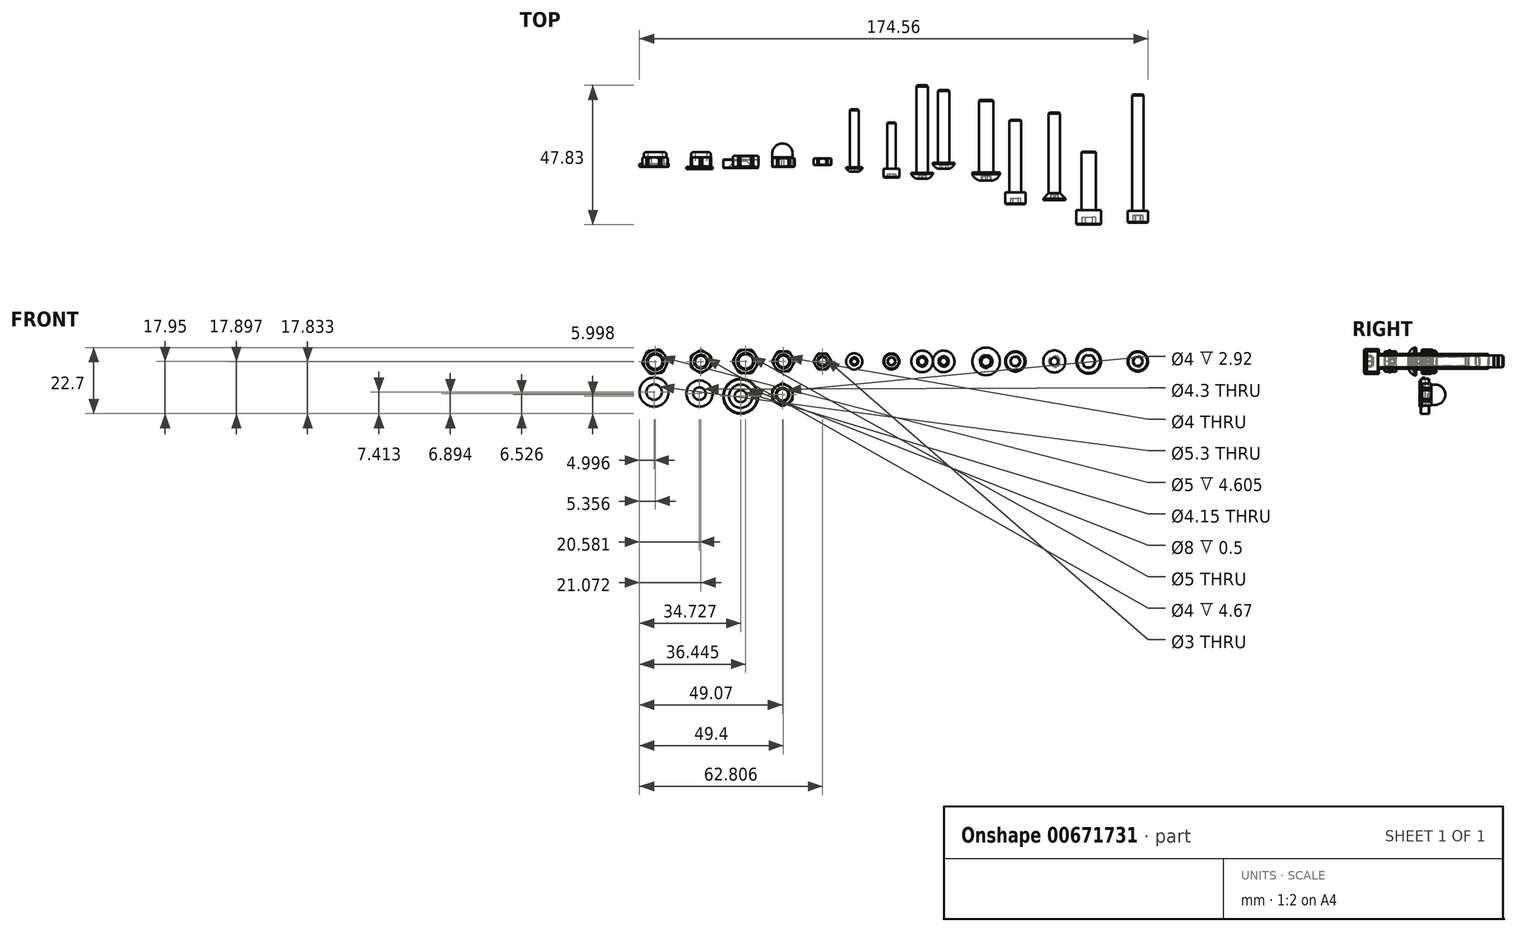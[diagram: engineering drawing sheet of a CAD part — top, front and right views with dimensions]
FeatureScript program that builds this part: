
annotation { "Feature Type Name" : "Feature", "Feature Type Description" : "" }
export const myFeature = defineFeature(function(context is Context, id is Id, definition is map)
    precondition{}
    {
        {
            var Q0;
            Q0=qCreatedBy(makeId("Top.planeOp"),FACE);
            var sketch = newSketch(context, id + "F0", { "sketchPlane" : qUnion([Q0])});
            skLineSegment(sketch, "E0.bottom", {"start": v(-2, 0) * mm, "end": v(-3.83, 0) * mm});
            skLineSegment(sketch, "E0.top", {"start": v(-2, 3) * mm, "end": v(-3.83, 3) * mm});
            skLineSegment(sketch, "E0.left", {"start": v(-2, 0) * mm, "end": v(-2, 3) * mm});
            skLineSegment(sketch, "E0.right", {"start": v(-3.83, 0) * mm, "end": v(-3.83, 3) * mm});
            skLineSegment(sketch, "E1", {"start": v(-2, 0) * mm, "end": v(0, 0) * mm, "construction": true});
            skLineSegment(sketch, "E2", {"start": v(0, 0) * mm, "end": v(0, 3) * mm, "construction": true});
            skSolve(sketch);
        }
        {
            var Q0;
            Q0=qSketchRegion(id+"F0",true);
            var Q1;
            Q1=sQuery(id+"F0.wireOp",EDGE,"E2");
            revolve(context, id + "F1", {"entities" : qUnion([Q0]), "axis" : qUnion([Q1]), "revolveType" : RevolveType.FULL});
        }
        {
            var Q0;
            Q0=makeQuery(id+"F1.opRevolve","SWEPT_EDGE",EDGE,{"disambiguationData":[OSD([sQuery(id+"F0.wireOp",EDGE,"E0.bottom"),sQuery(id+"F0.wireOp",EDGE,"E0.right")])]});
            var Q1;
            Q1=makeQuery(id+"F1.opRevolve","SWEPT_EDGE",EDGE,{"disambiguationData":[OSD([sQuery(id+"F0.wireOp",EDGE,"E0.top"),sQuery(id+"F0.wireOp",EDGE,"E0.right")])]});
            var Q2;
            Q2=makeQuery(id+"F1.opRevolve","SWEPT_EDGE",EDGE,{"disambiguationData":[OSD([sQuery(id+"F0.wireOp",EDGE,"E0.bottom"),sQuery(id+"F0.wireOp",EDGE,"E0.left")])]});
            var Q3;
            Q3=makeQuery(id+"F1.opRevolve","SWEPT_EDGE",EDGE,{"disambiguationData":[OSD([sQuery(id+"F0.wireOp",EDGE,"E0.top"),sQuery(id+"F0.wireOp",EDGE,"E0.left")])]});
            chamfer(context, id + "F2", {"entities" : qUnion([Q0, Q1, Q2, Q3]), "chamferType" : ChamferType.OFFSET_ANGLE, "width" : 0.77 * mm / 2, "oppositeDirection" : false, "angle" : 30 * degree, "tangentPropagation" : true});
        }
        {
            var Q0;
            Q0=makeQuery(id+"F1.opRevolve","SWEPT_FACE",FACE,{"disambiguationData":[OSD([sQuery(id+"F0.wireOp",EDGE,"E0.bottom")])]});
            var sketch = newSketch(context, id + "F3", { "sketchPlane" : qUnion([Q0])});
            skCircle(sketch, "E3.cCircle", {"center": v(0, 0) * mm, "radius": 3.45 * mm, "construction": true});
            skLineSegment(sketch, "E3.0", {"start": v(3.98, 0) * mm, "end": v(2, -3.45) * mm});
            skLineSegment(sketch, "E3.1", {"start": v(2, -3.45) * mm, "end": v(-2, -3.45) * mm});
            skLineSegment(sketch, "E3.2", {"start": v(-2, -3.45) * mm, "end": v(-3.98, 0) * mm});
            skLineSegment(sketch, "E3.3", {"start": v(-3.98, 0) * mm, "end": v(-2, 3.45) * mm});
            skLineSegment(sketch, "E3.4", {"start": v(-2, 3.45) * mm, "end": v(2, 3.45) * mm});
            skLineSegment(sketch, "E3.5", {"start": v(2, 3.45) * mm, "end": v(3.98, 0) * mm});
            skPoint(sketch, "E3.0.midPoint", {"position": v(2.99, -1.73) * mm});
            skCircle(sketch, "E4", {"center": v(0, 0) * mm, "radius": 4.53 * mm});
            skSolve(sketch);
        }
        {
            var Q0;
            Q0=qSketchRegion(id+"F3",true);
            extrude(context, id + "F4", {"entities" : qUnion([Q0]), "operationType" : NewBodyOperationType.REMOVE, "oppositeDirection" : true, "depth" : 25 * mm, "offsetDistance" : 25 * mm});
        }
        {
            var Q0;
            Q0=qCreatedBy(makeId("Top.planeOp"),FACE);
            var sketch = newSketch(context, id + "F5", { "sketchPlane" : qUnion([Q0])});
            skLineSegment(sketch, "E5.bottom", {"start": v(10.4, 2.85) * mm, "end": v(11.9, 2.85) * mm});
            skLineSegment(sketch, "E5.top", {"start": v(10.4, 0.58) * mm, "end": v(11.9, 0.58) * mm});
            skLineSegment(sketch, "E5.left", {"start": v(10.4, 2.85) * mm, "end": v(10.4, 0.58) * mm});
            skLineSegment(sketch, "E5.right", {"start": v(11.9, 2.85) * mm, "end": v(11.9, 0.58) * mm});
            skLineSegment(sketch, "E6", {"start": v(11.9, 0.58) * mm, "end": v(13.4, 0.58) * mm, "construction": true});
            skLineSegment(sketch, "E7", {"start": v(13.4, 0.58) * mm, "end": v(13.4, 2.85) * mm, "construction": true});
            skSolve(sketch);
        }
        {
            var Q0;
            Q0=qSketchRegion(id+"F5",true);
            var Q1;
            Q1=sQuery(id+"F5.wireOp",EDGE,"E7");
            revolve(context, id + "F6", {"entities" : qUnion([Q0]), "axis" : qUnion([Q1]), "revolveType" : RevolveType.FULL});
        }
        {
            var Q0;
            Q0=makeQuery(id+"F6.opRevolve","SWEPT_EDGE",EDGE,{"disambiguationData":[OSD([sQuery(id+"F5.wireOp",EDGE,"E5.top"),sQuery(id+"F5.wireOp",EDGE,"E5.right")])]});
            var Q1;
            Q1=makeQuery(id+"F6.opRevolve","SWEPT_EDGE",EDGE,{"disambiguationData":[OSD([sQuery(id+"F5.wireOp",EDGE,"E5.top"),sQuery(id+"F5.wireOp",EDGE,"E5.left")])]});
            var Q2;
            Q2=makeQuery(id+"F6.opRevolve","SWEPT_EDGE",EDGE,{"disambiguationData":[OSD([sQuery(id+"F5.wireOp",EDGE,"E5.bottom"),sQuery(id+"F5.wireOp",EDGE,"E5.right")])]});
            var Q3;
            Q3=makeQuery(id+"F6.opRevolve","SWEPT_EDGE",EDGE,{"disambiguationData":[OSD([sQuery(id+"F5.wireOp",EDGE,"E5.bottom"),sQuery(id+"F5.wireOp",EDGE,"E5.left")])]});
            chamfer(context, id + "F7", {"entities" : qUnion([Q0, Q1, Q2, Q3]), "width" : 0.51 / 2 * mm, "tangentPropagation" : true});
        }
        {
            var Q0;
            Q0=makeQuery(id+"F6.opRevolve","SWEPT_FACE",FACE,{"disambiguationData":[OSD([sQuery(id+"F5.wireOp",EDGE,"E5.top")])]});
            var sketch = newSketch(context, id + "F8", { "sketchPlane" : qUnion([Q0])});
            skCircle(sketch, "E8.cCircle", {"center": v(13.4, 0) * mm, "radius": 2.75 * mm, "construction": true});
            skLineSegment(sketch, "E8.0", {"start": v(16.58, 0) * mm, "end": v(15, -2.75) * mm});
            skLineSegment(sketch, "E8.1", {"start": v(15, -2.75) * mm, "end": v(11.82, -2.75) * mm});
            skLineSegment(sketch, "E8.2", {"start": v(11.82, -2.75) * mm, "end": v(10.23, 0) * mm});
            skLineSegment(sketch, "E8.3", {"start": v(10.23, 0) * mm, "end": v(11.82, 2.75) * mm});
            skLineSegment(sketch, "E8.4", {"start": v(11.82, 2.75) * mm, "end": v(15, 2.75) * mm});
            skLineSegment(sketch, "E8.5", {"start": v(15, 2.75) * mm, "end": v(16.58, 0) * mm});
            skPoint(sketch, "E8.0.midPoint", {"position": v(15.79, -1.38) * mm});
            skCircle(sketch, "E9", {"center": v(13.4, 0) * mm, "radius": 3.66 * mm});
            skSolve(sketch);
        }
        {
            var Q0;
            Q0=qSketchRegion(id+"F8",true);
            extrude(context, id + "F9", {"entities" : qUnion([Q0]), "operationType" : NewBodyOperationType.REMOVE, "oppositeDirection" : true, "depth" : 25 * mm, "offsetDistance" : 25 * mm});
        }
        {
            var Q0;
            Q0=qCreatedBy(makeId("Top.planeOp"),FACE);
            var sketch = newSketch(context, id + "F10", { "sketchPlane" : qUnion([Q0])});
            skLineSegment(sketch, "E10.bottom", {"start": v(-15.45, 3.8) * mm, "end": v(-17.35, 3.8) * mm});
            skLineSegment(sketch, "E10.top", {"start": v(-15.45, -0.05) * mm, "end": v(-17.35, -0.05) * mm});
            skLineSegment(sketch, "E10.left", {"start": v(-15.45, 3.8) * mm, "end": v(-15.45, -0.05) * mm});
            skLineSegment(sketch, "E10.right", {"start": v(-17.35, 3.8) * mm, "end": v(-17.35, -0.05) * mm});
            skLineSegment(sketch, "E11", {"start": v(-15.45, 3.8) * mm, "end": v(-12.95, 3.8) * mm, "construction": true});
            skLineSegment(sketch, "E12", {"start": v(-12.95, 3.8) * mm, "end": v(-12.95, -0.05) * mm, "construction": true});
            skSolve(sketch);
        }
        {
            var Q0;
            Q0=qSketchRegion(id+"F10",true);
            var Q1;
            Q1=sQuery(id+"F10.wireOp",EDGE,"E12");
            revolve(context, id + "F11", {"entities" : qUnion([Q0]), "axis" : qUnion([Q1]), "revolveType" : RevolveType.FULL});
        }
        {
            var Q0;
            Q0=makeQuery(id+"F11.opRevolve","SWEPT_EDGE",EDGE,{"disambiguationData":[OSD([sQuery(id+"F10.wireOp",EDGE,"E10.bottom"),sQuery(id+"F10.wireOp",EDGE,"E10.left")])]});
            var Q1;
            Q1=makeQuery(id+"F11.opRevolve","SWEPT_EDGE",EDGE,{"disambiguationData":[OSD([sQuery(id+"F10.wireOp",EDGE,"E10.bottom"),sQuery(id+"F10.wireOp",EDGE,"E10.right")])]});
            var Q2;
            Q2=makeQuery(id+"F11.opRevolve","SWEPT_EDGE",EDGE,{"disambiguationData":[OSD([sQuery(id+"F10.wireOp",EDGE,"E10.top"),sQuery(id+"F10.wireOp",EDGE,"E10.left")])]});
            var Q3;
            Q3=makeQuery(id+"F11.opRevolve","SWEPT_EDGE",EDGE,{"disambiguationData":[OSD([sQuery(id+"F10.wireOp",EDGE,"E10.top"),sQuery(id+"F10.wireOp",EDGE,"E10.right")])]});
            chamfer(context, id + "F12", {"entities" : qUnion([Q0, Q1, Q2, Q3]), "width" : 0.4 * mm, "tangentPropagation" : true});
        }
        {
            var Q0;
            Q0=makeQuery(id+"F11.opRevolve","SWEPT_FACE",FACE,{"disambiguationData":[OSD([sQuery(id+"F10.wireOp",EDGE,"E10.top")])]});
            var sketch = newSketch(context, id + "F13", { "sketchPlane" : qUnion([Q0])});
            skCircle(sketch, "E13.cCircle", {"center": v(-12.95, 0) * mm, "radius": 4 * mm, "construction": true});
            skLineSegment(sketch, "E13.0", {"start": v(-8.34, 0) * mm, "end": v(-10.65, -4) * mm});
            skLineSegment(sketch, "E13.1", {"start": v(-10.65, -4) * mm, "end": v(-15.26, -4) * mm});
            skLineSegment(sketch, "E13.2", {"start": v(-15.26, -4) * mm, "end": v(-17.57, 0) * mm});
            skLineSegment(sketch, "E13.3", {"start": v(-17.57, 0) * mm, "end": v(-15.26, 4) * mm});
            skLineSegment(sketch, "E13.4", {"start": v(-15.26, 4) * mm, "end": v(-10.65, 4) * mm});
            skLineSegment(sketch, "E13.5", {"start": v(-10.65, 4) * mm, "end": v(-8.34, 0) * mm});
            skPoint(sketch, "E13.0.midPoint", {"position": v(-9.5, -2) * mm});
            skCircle(sketch, "E14", {"center": v(-12.95, 0) * mm, "radius": 5.32 * mm});
            skSolve(sketch);
        }
        {
            var Q0;
            Q0=qSketchRegion(id+"F13",true);
            extrude(context, id + "F14", {"entities" : qUnion([Q0]), "operationType" : NewBodyOperationType.REMOVE, "oppositeDirection" : true, "depth" : 25 * mm, "offsetDistance" : 25 * mm});
        }
        {
            var Q0;
            Q0=qCreatedBy(makeId("Top.planeOp"),FACE);
            var sketch = newSketch(context, id + "F15", { "sketchPlane" : qUnion([Q0])});
            skLineSegment(sketch, "E15", {"start": v(24.32, 19.82) * mm, "end": v(24.32, -1.7) * mm});
            skLineSegment(sketch, "E16", {"start": v(24.32, -1.7) * mm, "end": v(22.95, -1.7) * mm});
            skLineSegment(sketch, "E17", {"start": v(21.55, -0.58) * mm, "end": v(21.55, -0.18) * mm});
            skLineSegment(sketch, "E18", {"start": v(21.55, -0.18) * mm, "end": v(22.82, -0.18) * mm});
            skLineSegment(sketch, "E19", {"start": v(22.82, -0.18) * mm, "end": v(22.82, 19.41) * mm});
            skLineSegment(sketch, "E20", {"start": v(22.82, 19.41) * mm, "end": v(23.18, 19.82) * mm});
            skLineSegment(sketch, "E21", {"start": v(23.18, 19.82) * mm, "end": v(24.32, 19.82) * mm});
            skArc(sketch, "E22", {"start": v(22.95, -1.7) * mm, "mid": v(22.16, -1.26) * mm, "end": v(21.55, -0.58) * mm});
            skSolve(sketch);
        }
        {
            var Q0;
            Q0=qSketchRegion(id+"F15",true);
            var Q1;
            Q1=sQuery(id+"F15.wireOp",EDGE,"E15");
            revolve(context, id + "F16", {"entities" : qUnion([Q0]), "axis" : qUnion([Q1]), "revolveType" : RevolveType.FULL});
        }
        {
            var Q0;
            Q0=makeQuery(id+"F16.opRevolve","SWEPT_FACE",FACE,{"disambiguationData":[OSD([sQuery(id+"F15.wireOp",EDGE,"E16")])]});
            var sketch = newSketch(context, id + "F17", { "sketchPlane" : qUnion([Q0])});
            skCircle(sketch, "E23.cCircle", {"center": v(24.32, 0) * mm, "radius": 1.02 * mm, "construction": true});
            skLineSegment(sketch, "E23.0", {"start": v(25.34, 0.59) * mm, "end": v(25.34, -0.59) * mm});
            skLineSegment(sketch, "E23.1", {"start": v(25.34, -0.59) * mm, "end": v(24.32, -1.17) * mm});
            skLineSegment(sketch, "E23.2", {"start": v(24.32, -1.17) * mm, "end": v(23.3, -0.59) * mm});
            skLineSegment(sketch, "E23.3", {"start": v(23.3, -0.59) * mm, "end": v(23.3, 0.59) * mm});
            skLineSegment(sketch, "E23.4", {"start": v(23.3, 0.59) * mm, "end": v(24.32, 1.17) * mm});
            skLineSegment(sketch, "E23.5", {"start": v(24.32, 1.17) * mm, "end": v(25.34, 0.59) * mm});
            skPoint(sketch, "E23.0.midPoint", {"position": v(25.34, 0) * mm});
            skSolve(sketch);
        }
        {
            var Q0;
            Q0=qSketchRegion(id+"F17",true);
            extrude(context, id + "F18", {"entities" : qUnion([Q0]), "operationType" : NewBodyOperationType.REMOVE, "oppositeDirection" : true, "depth" : 1.04 * mm, "offsetDistance" : 25 * mm});
        }
        {
            var Q0;
            Q0=qCreatedBy(makeId("Top.planeOp"),FACE);
            var sketch = newSketch(context, id + "F19", { "sketchPlane" : qUnion([Q0])});
            skLineSegment(sketch, "E24.bottom", {"start": v(34.33, -0.72) * mm, "end": v(35.58, -0.72) * mm});
            skLineSegment(sketch, "E24.top", {"start": v(34.61, -3.72) * mm, "end": v(37.08, -3.72) * mm});
            skLineSegment(sketch, "E24.left", {"start": v(34.33, -0.72) * mm, "end": v(34.33, -3.44) * mm});
            skLineSegment(sketch, "E24.right", {"start": v(37.08, -0.72) * mm, "end": v(37.08, -3.72) * mm});
            skLineSegment(sketch, "E25.top", {"start": v(37.08, 15.2) * mm, "end": v(35.86, 15.2) * mm});
            skLineSegment(sketch, "E25.left", {"start": v(37.08, -0.72) * mm, "end": v(37.08, 15.2) * mm});
            skLineSegment(sketch, "E25.right", {"start": v(35.58, -0.72) * mm, "end": v(35.58, 14.92) * mm});
            skLineSegment(sketch, "E26", {"start": v(34.33, -3.44) * mm, "end": v(34.61, -3.72) * mm});
            skLineSegment(sketch, "E27", {"start": v(35.58, 14.92) * mm, "end": v(35.86, 15.2) * mm});
            skSolve(sketch);
        }
        {
            var Q0;
            Q0=qSketchRegion(id+"F19",true);
            var Q1;
            Q1=sQuery(id+"F19.wireOp",EDGE,"E25.left");
            revolve(context, id + "F20", {"entities" : qUnion([Q0]), "axis" : qUnion([Q1]), "revolveType" : RevolveType.FULL});
        }
        {
            var Q0;
            Q0=makeQuery(id+"F20.opRevolve","SWEPT_FACE",FACE,{"disambiguationData":[OSD([sQuery(id+"F19.wireOp",EDGE,"E24.top")])]});
            var sketch = newSketch(context, id + "F21", { "sketchPlane" : qUnion([Q0])});
            skCircle(sketch, "E28.cCircle", {"center": v(37.08, 0) * mm, "radius": 1.25 * mm, "construction": true});
            skLineSegment(sketch, "E28.0", {"start": v(37.8, 1.25) * mm, "end": v(38.52, 0) * mm});
            skLineSegment(sketch, "E28.1", {"start": v(38.52, 0) * mm, "end": v(37.8, -1.25) * mm});
            skLineSegment(sketch, "E28.2", {"start": v(37.8, -1.25) * mm, "end": v(36.36, -1.25) * mm});
            skLineSegment(sketch, "E28.3", {"start": v(36.36, -1.25) * mm, "end": v(35.64, 0) * mm});
            skLineSegment(sketch, "E28.4", {"start": v(35.64, 0) * mm, "end": v(36.36, 1.25) * mm});
            skLineSegment(sketch, "E28.5", {"start": v(36.36, 1.25) * mm, "end": v(37.8, 1.25) * mm});
            skPoint(sketch, "E28.0.midPoint", {"position": v(38.16, 0.62) * mm});
            skSolve(sketch);
        }
        {
            var Q0;
            Q0=qSketchRegion(id+"F21",true);
            extrude(context, id + "F22", {"entities" : qUnion([Q0]), "operationType" : NewBodyOperationType.REMOVE, "oppositeDirection" : true, "depth" : 1.3 * mm, "offsetDistance" : 25 * mm});
        }
        {
            var Q0;
            Q0=qCreatedBy(makeId("Top.planeOp"),FACE);
            var sketch = newSketch(context, id + "F23", { "sketchPlane" : qUnion([Q0])});
            skLineSegment(sketch, "E29", {"start": v(55, 26.35) * mm, "end": v(55, -0.73) * mm});
            skLineSegment(sketch, "E30", {"start": v(55, -0.73) * mm, "end": v(53.25, -0.73) * mm});
            skLineSegment(sketch, "E31", {"start": v(51.3, 0.95) * mm, "end": v(51.3, 1.35) * mm});
            skLineSegment(sketch, "E32", {"start": v(51.3, 1.35) * mm, "end": v(53, 1.35) * mm});
            skLineSegment(sketch, "E33", {"start": v(53, 1.35) * mm, "end": v(53, 25.94) * mm});
            skLineSegment(sketch, "E34", {"start": v(53, 25.94) * mm, "end": v(53.36, 26.35) * mm});
            skLineSegment(sketch, "E35", {"start": v(53.36, 26.35) * mm, "end": v(55, 26.35) * mm});
            skArc(sketch, "E36", {"start": v(53.25, -0.73) * mm, "mid": v(52.07, -0.12) * mm, "end": v(51.3, 0.95) * mm});
            skSolve(sketch);
        }
        {
            var Q0;
            Q0=qSketchRegion(id+"F23",true);
            var Q1;
            Q1=sQuery(id+"F23.wireOp",EDGE,"E29");
            revolve(context, id + "F24", {"entities" : qUnion([Q0]), "axis" : qUnion([Q1]), "revolveType" : RevolveType.FULL});
        }
        {
            var Q0;
            Q0=makeQuery(id+"F24.opRevolve","SWEPT_FACE",FACE,{"disambiguationData":[OSD([sQuery(id+"F23.wireOp",EDGE,"E30")])]});
            var sketch = newSketch(context, id + "F25", { "sketchPlane" : qUnion([Q0])});
            skCircle(sketch, "E37.cCircle", {"center": v(55, 0) * mm, "radius": 1.27 * mm, "construction": true});
            skLineSegment(sketch, "E37.0", {"start": v(56.47, 0) * mm, "end": v(55.73, -1.27) * mm});
            skLineSegment(sketch, "E37.1", {"start": v(55.73, -1.27) * mm, "end": v(54.27, -1.27) * mm});
            skLineSegment(sketch, "E37.2", {"start": v(54.27, -1.27) * mm, "end": v(53.53, 0) * mm});
            skLineSegment(sketch, "E37.3", {"start": v(53.53, 0) * mm, "end": v(54.27, 1.27) * mm});
            skLineSegment(sketch, "E37.4", {"start": v(54.27, 1.27) * mm, "end": v(55.73, 1.27) * mm});
            skLineSegment(sketch, "E37.5", {"start": v(55.73, 1.27) * mm, "end": v(56.47, 0) * mm});
            skPoint(sketch, "E37.0.midPoint", {"position": v(56.1, -0.64) * mm});
            skSolve(sketch);
        }
        {
            var Q0;
            Q0=qSketchRegion(id+"F25",true);
            extrude(context, id + "F26", {"entities" : qUnion([Q0]), "operationType" : NewBodyOperationType.REMOVE, "oppositeDirection" : true, "depth" : 1.3 * mm, "offsetDistance" : 25 * mm});
        }
        {
            var Q0;
            Q0=qCreatedBy(makeId("Top.planeOp"),FACE);
            var sketch = newSketch(context, id + "F27", { "sketchPlane" : qUnion([Q0])});
            skLineSegment(sketch, "E38.bottom", {"start": v(76.11, -8.88) * mm, "end": v(77.61, -8.88) * mm});
            skLineSegment(sketch, "E38.top", {"start": v(76.4, -12.88) * mm, "end": v(79.61, -12.88) * mm});
            skLineSegment(sketch, "E38.left", {"start": v(76.11, -8.88) * mm, "end": v(76.11, -12.6) * mm});
            skLineSegment(sketch, "E38.right", {"start": v(79.61, -8.88) * mm, "end": v(79.61, -12.88) * mm});
            skLineSegment(sketch, "E39.top", {"start": v(79.61, 16.12) * mm, "end": v(77.9, 16.12) * mm});
            skLineSegment(sketch, "E39.left", {"start": v(79.61, -8.88) * mm, "end": v(79.61, 16.12) * mm});
            skLineSegment(sketch, "E39.right", {"start": v(77.61, -8.88) * mm, "end": v(77.61, 15.84) * mm});
            skLineSegment(sketch, "E40", {"start": v(76.11, -12.6) * mm, "end": v(76.4, -12.88) * mm});
            skLineSegment(sketch, "E41", {"start": v(77.61, 15.84) * mm, "end": v(77.9, 16.12) * mm});
            skSolve(sketch);
        }
        {
            var Q0;
            Q0=qSketchRegion(id+"F27",true);
            var Q1;
            Q1=sQuery(id+"F27.wireOp",EDGE,"E39.left");
            revolve(context, id + "F28", {"entities" : qUnion([Q0]), "axis" : qUnion([Q1]), "revolveType" : RevolveType.FULL});
        }
        {
            var Q0;
            Q0=makeQuery(id+"F28.opRevolve","SWEPT_FACE",FACE,{"disambiguationData":[OSD([sQuery(id+"F27.wireOp",EDGE,"E38.top")])]});
            var sketch = newSketch(context, id + "F29", { "sketchPlane" : qUnion([Q0])});
            skCircle(sketch, "E42.cCircle", {"center": v(79.61, 0) * mm, "radius": 1.5 * mm, "construction": true});
            skLineSegment(sketch, "E42.0", {"start": v(81.34, 0) * mm, "end": v(80.48, -1.5) * mm});
            skLineSegment(sketch, "E42.1", {"start": v(80.48, -1.5) * mm, "end": v(78.75, -1.5) * mm});
            skLineSegment(sketch, "E42.2", {"start": v(78.75, -1.5) * mm, "end": v(77.88, 0) * mm});
            skLineSegment(sketch, "E42.3", {"start": v(77.88, 0) * mm, "end": v(78.75, 1.5) * mm});
            skLineSegment(sketch, "E42.4", {"start": v(78.75, 1.5) * mm, "end": v(80.48, 1.5) * mm});
            skLineSegment(sketch, "E42.5", {"start": v(80.48, 1.5) * mm, "end": v(81.34, 0) * mm});
            skPoint(sketch, "E42.0.midPoint", {"position": v(80.91, -0.75) * mm});
            skSolve(sketch);
        }
        {
            var Q0;
            Q0=qSketchRegion(id+"F29",true);
            extrude(context, id + "F30", {"entities" : qUnion([Q0]), "operationType" : NewBodyOperationType.REMOVE, "oppositeDirection" : true, "depth" : 2 * mm, "offsetDistance" : 25 * mm});
        }
        {
            var Q0;
            Q0=qCreatedBy(makeId("Top.planeOp"),FACE);
            var sketch = newSketch(context, id + "F31", { "sketchPlane" : qUnion([Q0])});
            skLineSegment(sketch, "E43.bottom", {"start": v(100.55, -14.88) * mm, "end": v(102.3, -14.88) * mm});
            skLineSegment(sketch, "E43.top", {"start": v(100.83, -19.88) * mm, "end": v(104.8, -19.88) * mm});
            skLineSegment(sketch, "E43.left", {"start": v(100.55, -14.88) * mm, "end": v(100.55, -19.6) * mm});
            skLineSegment(sketch, "E43.right", {"start": v(104.8, -14.88) * mm, "end": v(104.8, -19.88) * mm});
            skLineSegment(sketch, "E44.top", {"start": v(104.8, 5.12) * mm, "end": v(102.58, 5.12) * mm});
            skLineSegment(sketch, "E44.left", {"start": v(104.8, -14.88) * mm, "end": v(104.8, 5.12) * mm});
            skLineSegment(sketch, "E44.right", {"start": v(102.3, -14.88) * mm, "end": v(102.3, 4.84) * mm});
            skLineSegment(sketch, "E45", {"start": v(100.55, -19.6) * mm, "end": v(100.83, -19.88) * mm});
            skLineSegment(sketch, "E46", {"start": v(102.3, 4.84) * mm, "end": v(102.58, 5.12) * mm});
            skSolve(sketch);
        }
        {
            var Q0;
            Q0=qSketchRegion(id+"F31",true);
            var Q1;
            Q1=sQuery(id+"F31.wireOp",EDGE,"E43.right");
            revolve(context, id + "F32", {"entities" : qUnion([Q0]), "axis" : qUnion([Q1]), "revolveType" : RevolveType.FULL});
        }
        {
            var Q0;
            Q0=makeQuery(id+"F32.opRevolve","SWEPT_FACE",FACE,{"disambiguationData":[OSD([sQuery(id+"F31.wireOp",EDGE,"E43.top")])]});
            var sketch = newSketch(context, id + "F33", { "sketchPlane" : qUnion([Q0])});
            skCircle(sketch, "E47.cCircle", {"center": v(104.8, 0) * mm, "radius": 2 * mm, "construction": true});
            skLineSegment(sketch, "E47.0", {"start": v(107.1, 0) * mm, "end": v(105.95, -2) * mm});
            skLineSegment(sketch, "E47.1", {"start": v(105.95, -2) * mm, "end": v(103.64, -2) * mm});
            skLineSegment(sketch, "E47.2", {"start": v(103.64, -2) * mm, "end": v(102.49, 0) * mm});
            skLineSegment(sketch, "E47.3", {"start": v(102.49, 0) * mm, "end": v(103.64, 2) * mm});
            skLineSegment(sketch, "E47.4", {"start": v(103.64, 2) * mm, "end": v(105.95, 2) * mm});
            skLineSegment(sketch, "E47.5", {"start": v(105.95, 2) * mm, "end": v(107.1, 0) * mm});
            skPoint(sketch, "E47.0.midPoint", {"position": v(106.53, -1) * mm});
            skSolve(sketch);
        }
        {
            var Q0;
            Q0=qSketchRegion(id+"F33",true);
            extrude(context, id + "F34", {"entities" : qUnion([Q0]), "operationType" : NewBodyOperationType.REMOVE, "oppositeDirection" : true, "depth" : 2.5 * mm, "offsetDistance" : 25 * mm});
        }
        {
            var Q0;
            Q0=qCreatedBy(makeId("Top.planeOp"),FACE);
            var sketch = newSketch(context, id + "F35", { "sketchPlane" : qUnion([Q0])});
            skLineSegment(sketch, "E48.bottom", {"start": v(118.16, -15.2) * mm, "end": v(119.66, -15.2) * mm});
            skLineSegment(sketch, "E48.top", {"start": v(118.45, -19.2) * mm, "end": v(121.66, -19.2) * mm});
            skLineSegment(sketch, "E48.left", {"start": v(118.16, -15.2) * mm, "end": v(118.16, -18.93) * mm});
            skLineSegment(sketch, "E48.right", {"start": v(121.66, -15.2) * mm, "end": v(121.66, -19.2) * mm});
            skLineSegment(sketch, "E49.top", {"start": v(121.66, 24.8) * mm, "end": v(119.95, 24.8) * mm});
            skLineSegment(sketch, "E49.left", {"start": v(121.66, -15.2) * mm, "end": v(121.66, 24.8) * mm});
            skLineSegment(sketch, "E49.right", {"start": v(119.66, -15.2) * mm, "end": v(119.66, 24.5) * mm});
            skLineSegment(sketch, "E50", {"start": v(118.16, -18.93) * mm, "end": v(118.45, -19.2) * mm});
            skLineSegment(sketch, "E51", {"start": v(119.66, 24.5) * mm, "end": v(119.95, 24.8) * mm});
            skSolve(sketch);
        }
        {
            var Q0;
            Q0=qSketchRegion(id+"F35",true);
            var Q1;
            Q1=sQuery(id+"F35.wireOp",EDGE,"E49.left");
            revolve(context, id + "F36", {"entities" : qUnion([Q0]), "axis" : qUnion([Q1]), "revolveType" : RevolveType.FULL});
        }
        {
            var Q0;
            Q0=makeQuery(id+"F36.opRevolve","SWEPT_FACE",FACE,{"disambiguationData":[OSD([sQuery(id+"F35.wireOp",EDGE,"E48.top")])]});
            var sketch = newSketch(context, id + "F37", { "sketchPlane" : qUnion([Q0])});
            skCircle(sketch, "E52.cCircle", {"center": v(121.66, 0) * mm, "radius": 1.5 * mm, "construction": true});
            skLineSegment(sketch, "E52.0", {"start": v(122.62, 1.44) * mm, "end": v(123.4, -0.1) * mm});
            skLineSegment(sketch, "E52.1", {"start": v(123.4, -0.1) * mm, "end": v(122.43, -1.55) * mm});
            skLineSegment(sketch, "E52.2", {"start": v(122.43, -1.55) * mm, "end": v(120.7, -1.44) * mm});
            skLineSegment(sketch, "E52.3", {"start": v(120.7, -1.44) * mm, "end": v(119.94, 0.1) * mm});
            skLineSegment(sketch, "E52.4", {"start": v(119.94, 0.1) * mm, "end": v(120.9, 1.55) * mm});
            skLineSegment(sketch, "E52.5", {"start": v(120.9, 1.55) * mm, "end": v(122.62, 1.44) * mm});
            skPoint(sketch, "E52.0.midPoint", {"position": v(123, 0.67) * mm});
            skSolve(sketch);
        }
        {
            var Q0;
            Q0=qSketchRegion(id+"F37",true);
            extrude(context, id + "F38", {"entities" : qUnion([Q0]), "operationType" : NewBodyOperationType.REMOVE, "oppositeDirection" : true, "depth" : 2.5 * mm, "offsetDistance" : 25 * mm});
        }
        {
            var Q0;
            Q0=qCreatedBy(makeId("Front.planeOp"),FACE);
            var sketch = newSketch(context, id + "F39", { "sketchPlane" : qUnion([Q0])});
            skCircle(sketch, "E53", {"center": v(-28.33, -0.05) * mm, "radius": 3.83 * mm});
            skCircle(sketch, "E54", {"center": v(-28.33, -0.05) * mm, "radius": 2 * mm});
            skSolve(sketch);
        }
        {
            var Q0;
            Q0=qSketchRegion(id+"F39",true);
            extrude(context, id + "F40", {"entities" : qUnion([Q0]), "oppositeDirection" : true, "depth" : 3.25 * mm, "offsetDistance" : 25 * mm});
        }
        {
            var Q0;
            Q0=makeQuery(id+"F40.opExtrude","CAP_EDGE",EDGE,{"disambiguationData":[OSD([sQuery(id+"F39.wireOp",EDGE,"E53")])],"isStart":false});
            var Q1;
            Q1=makeQuery(id+"F40.opExtrude","CAP_EDGE",EDGE,{"disambiguationData":[OSD([sQuery(id+"F39.wireOp",EDGE,"E53")])],"isStart":true});
            var Q2;
            Q2=makeQuery(id+"F40.opExtrude","CAP_EDGE",EDGE,{"disambiguationData":[OSD([sQuery(id+"F39.wireOp",EDGE,"E54")])],"isStart":true});
            chamfer(context, id + "F41", {"entities" : qUnion([Q0, Q1, Q2]), "width" : 0.66 / 2 * mm, "tangentPropagation" : true});
        }
        {
            var Q0;
            Q0=makeQuery(id+"F40.opExtrude","CAP_FACE",FACE,{"disambiguationData":[OSD([sQuery(id+"F39.wireOp",EDGE,"E53"),sQuery(id+"F39.wireOp",EDGE,"E54")])],"isStart":false});
            var sketch = newSketch(context, id + "F42", { "sketchPlane" : qUnion([Q0])});
            skCircle(sketch, "E55.cCircle", {"center": v(28.33, -0.05) * mm, "radius": 3.5 * mm, "construction": true});
            skLineSegment(sketch, "E55.0", {"start": v(31.83, 1.97) * mm, "end": v(31.83, -2.07) * mm});
            skLineSegment(sketch, "E55.1", {"start": v(31.83, -2.07) * mm, "end": v(28.33, -4.1) * mm});
            skLineSegment(sketch, "E55.2", {"start": v(28.33, -4.1) * mm, "end": v(24.83, -2.07) * mm});
            skLineSegment(sketch, "E55.3", {"start": v(24.83, -2.07) * mm, "end": v(24.83, 1.97) * mm});
            skLineSegment(sketch, "E55.4", {"start": v(24.83, 1.97) * mm, "end": v(28.33, 3.99) * mm});
            skLineSegment(sketch, "E55.5", {"start": v(28.33, 3.99) * mm, "end": v(31.83, 1.97) * mm});
            skPoint(sketch, "E55.0.midPoint", {"position": v(31.83, -0.05) * mm});
            skCircle(sketch, "E56", {"center": v(28.33, -0.05) * mm, "radius": 6.48 * mm});
            skSolve(sketch);
        }
        {
            var Q0;
            Q0=qSketchRegion(id+"F42",true);
            extrude(context, id + "F43", {"entities" : qUnion([Q0]), "operationType" : NewBodyOperationType.REMOVE, "oppositeDirection" : true, "depth" : 25 * mm, "offsetDistance" : 25 * mm});
        }
        {
            var Q0;
            Q0=makeQuery(id+"F40.opExtrude","CAP_FACE",FACE,{"disambiguationData":[OSD([sQuery(id+"F39.wireOp",EDGE,"E53"),sQuery(id+"F39.wireOp",EDGE,"E54")])],"isStart":false});
            var sketch = newSketch(context, id + "F44", { "sketchPlane" : qUnion([Q0])});
            skCircle(sketch, "E57", {"center": v(28.33, -0.05) * mm, "radius": 2 * mm});
            skCircle(sketch, "E58", {"center": v(28.33, -0.05) * mm, "radius": 3.38 * mm});
            skSolve(sketch);
        }
        {
            var Q0;
            Q0=qSketchRegion(id+"F44",true);
            extrude(context, id + "F45", {"entities" : qUnion([Q0]), "operationType" : NewBodyOperationType.ADD, "depth" : (5 - 3.25) * mm, "offsetDistance" : 25 * mm});
        }
        {
            var Q0;
            Q0=makeQuery(id+"F45.opExtrude","CAP_EDGE",EDGE,{"disambiguationData":[OSD([sQuery(id+"F44.wireOp",EDGE,"E58")])],"isStart":false});
            fillet(context, id + "F46", {"entities" : qUnion([Q0]), "radius" : 0.75 * mm, "tangentPropagation" : true, "allowEdgeOverflow" : false});
        }
        {
            var Q0;
            Q0=qCreatedBy(makeId("Top.planeOp"),FACE);
            var sketch = newSketch(context, id + "F47", { "sketchPlane" : qUnion([Q0])});
            skLineSegment(sketch, "E59", {"start": v(69.58, 22.98) * mm, "end": v(69.58, -4.77) * mm});
            skLineSegment(sketch, "E60", {"start": v(69.58, -4.77) * mm, "end": v(67.48, -4.77) * mm});
            skLineSegment(sketch, "E61", {"start": v(64.83, -2.62) * mm, "end": v(64.83, -2.02) * mm});
            skLineSegment(sketch, "E62", {"start": v(64.83, -2.02) * mm, "end": v(67.08, -2.02) * mm});
            skLineSegment(sketch, "E63", {"start": v(67.08, -2.02) * mm, "end": v(67.08, 22.58) * mm});
            skLineSegment(sketch, "E64", {"start": v(67.08, 22.58) * mm, "end": v(67.44, 22.98) * mm});
            skLineSegment(sketch, "E65", {"start": v(67.44, 22.98) * mm, "end": v(69.58, 22.98) * mm});
            skArc(sketch, "E66", {"start": v(67.48, -4.77) * mm, "mid": v(65.88, -4.03) * mm, "end": v(64.83, -2.62) * mm});
            skSolve(sketch);
        }
        {
            var Q0;
            Q0=makeQuery(id+"F47.imprint","IMPRINT",FACE,{"disambiguationData":[TD([[makeQuery(id+"F47.imprint","IMPRINT",EDGE,{"derivedFrom":sQuery(id+"F47.wireOp",EDGE,"E59")}),-1.0]])]});
            var Q1;
            Q1=sQuery(id+"F47.wireOp",EDGE,"E59");
            revolve(context, id + "F48", {"entities" : qUnion([Q0]), "axis" : qUnion([Q1]), "revolveType" : RevolveType.FULL});
        }
        {
            var Q0;
            Q0=makeQuery(id+"F48.opRevolve","SWEPT_FACE",FACE,{"disambiguationData":[OSD([sQuery(id+"F47.wireOp",EDGE,"E60")])]});
            var sketch = newSketch(context, id + "F49", { "sketchPlane" : qUnion([Q0])});
            skCircle(sketch, "E67.cCircle", {"center": v(69.58, 0) * mm, "radius": 1.5 * mm, "construction": true});
            skLineSegment(sketch, "E67.0", {"start": v(69.92, 1.7) * mm, "end": v(71.22, 0.55) * mm});
            skLineSegment(sketch, "E67.1", {"start": v(71.22, 0.55) * mm, "end": v(70.88, -1.14) * mm});
            skLineSegment(sketch, "E67.2", {"start": v(70.88, -1.14) * mm, "end": v(69.24, -1.7) * mm});
            skLineSegment(sketch, "E67.3", {"start": v(69.24, -1.7) * mm, "end": v(67.94, -0.55) * mm});
            skLineSegment(sketch, "E67.4", {"start": v(67.94, -0.55) * mm, "end": v(68.28, 1.14) * mm});
            skLineSegment(sketch, "E67.5", {"start": v(68.28, 1.14) * mm, "end": v(69.92, 1.7) * mm});
            skPoint(sketch, "E67.0.midPoint", {"position": v(70.57, 1.13) * mm});
            skSolve(sketch);
        }
        {
            var Q0;
            Q0=qSketchRegion(id+"F49",true);
            extrude(context, id + "F50", {"entities" : qUnion([Q0]), "operationType" : NewBodyOperationType.REMOVE, "oppositeDirection" : true, "depth" : 1.56 * mm, "offsetDistance" : 25 * mm});
        }
        {
            var Q0;
            Q0=qCreatedBy(makeId("Front.planeOp"),FACE);
            var sketch = newSketch(context, id + "F51", { "sketchPlane" : qUnion([Q0])});
            skCircle(sketch, "E68", {"center": v(-44.04, -0.12) * mm, "radius": 4.4 * mm});
            skCircle(sketch, "E69", {"center": v(-44.04, -0.12) * mm, "radius": 2.5 * mm});
            skSolve(sketch);
        }
        {
            var Q0;
            Q0=qSketchRegion(id+"F51",true);
            extrude(context, id + "F52", {"entities" : qUnion([Q0]), "oppositeDirection" : true, "depth" : 3.25 * mm, "offsetDistance" : 25 * mm});
        }
        {
            var Q0;
            Q0=makeQuery(id+"F52.opExtrude","CAP_EDGE",EDGE,{"disambiguationData":[OSD([sQuery(id+"F51.wireOp",EDGE,"E68")])],"isStart":false});
            var Q1;
            Q1=makeQuery(id+"F52.opExtrude","CAP_EDGE",EDGE,{"disambiguationData":[OSD([sQuery(id+"F51.wireOp",EDGE,"E68")])],"isStart":true});
            var Q2;
            Q2=makeQuery(id+"F52.opExtrude","CAP_EDGE",EDGE,{"disambiguationData":[OSD([sQuery(id+"F51.wireOp",EDGE,"E69")])],"isStart":true});
            chamfer(context, id + "F53", {"entities" : qUnion([Q0, Q1, Q2]), "width" : (0.79 / 2) * mm, "tangentPropagation" : true});
        }
        {
            var Q0;
            Q0=makeQuery(id+"F52.opExtrude","CAP_FACE",FACE,{"disambiguationData":[OSD([sQuery(id+"F51.wireOp",EDGE,"E68"),sQuery(id+"F51.wireOp",EDGE,"E69")])],"isStart":false});
            var sketch = newSketch(context, id + "F54", { "sketchPlane" : qUnion([Q0])});
            skCircle(sketch, "E70.cCircle", {"center": v(44.04, -0.12) * mm, "radius": 4 * mm, "construction": true});
            skLineSegment(sketch, "E70.0", {"start": v(39.46, 0.47) * mm, "end": v(42.26, 4.14) * mm});
            skLineSegment(sketch, "E70.1", {"start": v(42.26, 4.14) * mm, "end": v(46.84, 3.56) * mm});
            skLineSegment(sketch, "E70.2", {"start": v(46.84, 3.56) * mm, "end": v(48.63, -0.7) * mm});
            skLineSegment(sketch, "E70.3", {"start": v(48.63, -0.7) * mm, "end": v(45.83, -4.38) * mm});
            skLineSegment(sketch, "E70.4", {"start": v(45.83, -4.38) * mm, "end": v(41.25, -3.8) * mm});
            skLineSegment(sketch, "E70.5", {"start": v(41.25, -3.8) * mm, "end": v(39.46, 0.47) * mm});
            skPoint(sketch, "E70.0.midPoint", {"position": v(40.86, 2.3) * mm});
            skCircle(sketch, "E71", {"center": v(44.04, -0.12) * mm, "radius": 6.63 * mm});
            skSolve(sketch);
        }
        {
            var Q0;
            Q0=qSketchRegion(id+"F54",true);
            extrude(context, id + "F55", {"entities" : qUnion([Q0]), "operationType" : NewBodyOperationType.REMOVE, "oppositeDirection" : true, "depth" : 25 * mm, "offsetDistance" : 25 * mm});
        }
        {
            var Q0;
            Q0=makeQuery(id+"F52.opExtrude","CAP_FACE",FACE,{"disambiguationData":[OSD([sQuery(id+"F51.wireOp",EDGE,"E68"),sQuery(id+"F51.wireOp",EDGE,"E69")])],"isStart":false});
            var sketch = newSketch(context, id + "F56", { "sketchPlane" : qUnion([Q0])});
            skCircle(sketch, "E72", {"center": v(44.04, -0.12) * mm, "radius": 2.5 * mm});
            skCircle(sketch, "E73", {"center": v(44.04, -0.12) * mm, "radius": 3.88 * mm});
            skSolve(sketch);
        }
        {
            var Q0;
            Q0=qSketchRegion(id+"F56",true);
            extrude(context, id + "F57", {"entities" : qUnion([Q0]), "operationType" : NewBodyOperationType.ADD, "depth" : 1.75 * mm, "offsetDistance" : 25 * mm});
        }
        {
            var Q0;
            Q0=makeQuery(id+"F57.opExtrude","CAP_EDGE",EDGE,{"disambiguationData":[OSD([sQuery(id+"F56.wireOp",EDGE,"E73")])],"isStart":false});
            fillet(context, id + "F58", {"entities" : qUnion([Q0]), "radius" : 0.75 * mm, "tangentPropagation" : true, "allowEdgeOverflow" : false});
        }
        {
            var Q0;
            Q0=qCreatedBy(makeId("Front.planeOp"),FACE);
            var sketch = newSketch(context, id + "F59", { "sketchPlane" : qUnion([Q0])});
            skCircle(sketch, "E74", {"center": v(-44.4, -10.54) * mm, "radius": 2.65 * mm});
            skCircle(sketch, "E75", {"center": v(-44.4, -10.54) * mm, "radius": 5 * mm});
            skSolve(sketch);
        }
        {
            var Q0;
            Q0=qSketchRegion(id+"F59",true);
            extrude(context, id + "F60", {"entities" : qUnion([Q0]), "oppositeDirection" : true, "depth" : 1 * mm, "offsetDistance" : 25 * mm});
        }
        {
            var Q0;
            Q0=qCreatedBy(makeId("Top.planeOp"),FACE);
            var sketch = newSketch(context, id + "F61", { "sketchPlane" : qUnion([Q0])});
            skLineSegment(sketch, "E76", {"start": v(47.6, 27.95) * mm, "end": v(47.6, -4.13) * mm});
            skLineSegment(sketch, "E77", {"start": v(47.6, -4.13) * mm, "end": v(45.86, -4.13) * mm});
            skLineSegment(sketch, "E78", {"start": v(43.9, -2.45) * mm, "end": v(43.9, -2.05) * mm});
            skLineSegment(sketch, "E79", {"start": v(43.9, -2.05) * mm, "end": v(45.6, -2.05) * mm});
            skLineSegment(sketch, "E80", {"start": v(45.6, -2.05) * mm, "end": v(45.6, 27.54) * mm});
            skLineSegment(sketch, "E81", {"start": v(45.6, 27.54) * mm, "end": v(45.97, 27.95) * mm});
            skLineSegment(sketch, "E82", {"start": v(45.97, 27.95) * mm, "end": v(47.6, 27.95) * mm});
            skArc(sketch, "E83", {"start": v(45.86, -4.13) * mm, "mid": v(44.68, -3.53) * mm, "end": v(43.9, -2.45) * mm});
            skSolve(sketch);
        }
        {
            var Q0;
            Q0=makeQuery(id+"F61.imprint","IMPRINT",FACE,{"disambiguationData":[TD([[makeQuery(id+"F61.imprint","IMPRINT",EDGE,{"derivedFrom":sQuery(id+"F61.wireOp",EDGE,"E76")}),-1.0]])]});
            var Q1;
            Q1=sQuery(id+"F61.wireOp",EDGE,"E76");
            revolve(context, id + "F62", {"entities" : qUnion([Q0]), "axis" : qUnion([Q1]), "revolveType" : RevolveType.FULL});
        }
        {
            var Q0;
            Q0=makeQuery(id+"F62.opRevolve","SWEPT_FACE",FACE,{"disambiguationData":[OSD([sQuery(id+"F61.wireOp",EDGE,"E77")])]});
            var sketch = newSketch(context, id + "F63", { "sketchPlane" : qUnion([Q0])});
            skCircle(sketch, "E84.cCircle", {"center": v(47.6, 0) * mm, "radius": 1.25 * mm, "construction": true});
            skLineSegment(sketch, "E84.0", {"start": v(48.97, -0.48) * mm, "end": v(47.87, -1.42) * mm});
            skLineSegment(sketch, "E84.1", {"start": v(47.87, -1.42) * mm, "end": v(46.51, -0.94) * mm});
            skLineSegment(sketch, "E84.2", {"start": v(46.51, -0.94) * mm, "end": v(46.25, 0.48) * mm});
            skLineSegment(sketch, "E84.3", {"start": v(46.25, 0.48) * mm, "end": v(47.35, 1.42) * mm});
            skLineSegment(sketch, "E84.4", {"start": v(47.35, 1.42) * mm, "end": v(48.7, 0.94) * mm});
            skLineSegment(sketch, "E84.5", {"start": v(48.7, 0.94) * mm, "end": v(48.97, -0.48) * mm});
            skPoint(sketch, "E84.0.midPoint", {"position": v(48.42, -0.95) * mm});
            skSolve(sketch);
        }
        {
            var Q0;
            Q0=qSketchRegion(id+"F63",true);
            extrude(context, id + "F64", {"entities" : qUnion([Q0]), "operationType" : NewBodyOperationType.REMOVE, "oppositeDirection" : true, "depth" : 1.3 * mm, "offsetDistance" : 25 * mm});
        }
        {
            var Q0;
            Q0=qCreatedBy(makeId("Front.planeOp"),FACE);
            var sketch = newSketch(context, id + "F65", { "sketchPlane" : qUnion([Q0])});
            skCircle(sketch, "E85", {"center": v(-28.82, -11.06) * mm, "radius": 2.15 * mm});
            skCircle(sketch, "E86", {"center": v(-28.82, -11.06) * mm, "radius": 4.5 * mm});
            skSolve(sketch);
        }
        {
            var Q0;
            Q0=qSketchRegion(id+"F65",true);
            extrude(context, id + "F66", {"entities" : qUnion([Q0]), "depth" : 0.8 * mm, "offsetDistance" : 25 * mm});
        }
        {
            var Q0;
            Q0=qCreatedBy(makeId("Front.planeOp"),FACE);
            var sketch = newSketch(context, id + "F67", { "sketchPlane" : qUnion([Q0])});
            skCircle(sketch, "E87", {"center": v(-0.33, -11.42) * mm, "radius": 3.83 * mm});
            skCircle(sketch, "E88", {"center": v(-0.33, -11.42) * mm, "radius": 2 * mm});
            skSolve(sketch);
        }
        {
            var Q0;
            Q0=qSketchRegion(id+"F67",true);
            extrude(context, id + "F68", {"entities" : qUnion([Q0]), "oppositeDirection" : true, "depth" : 3.25 * mm, "offsetDistance" : 25 * mm});
        }
        {
            var Q0;
            Q0=makeQuery(id+"F68.opExtrude","CAP_EDGE",EDGE,{"disambiguationData":[OSD([sQuery(id+"F67.wireOp",EDGE,"E87")])],"isStart":true});
            var Q1;
            Q1=makeQuery(id+"F68.opExtrude","CAP_EDGE",EDGE,{"disambiguationData":[OSD([sQuery(id+"F67.wireOp",EDGE,"E88")])],"isStart":true});
            var Q2;
            Q2=makeQuery(id+"F68.opExtrude","CAP_EDGE",EDGE,{"disambiguationData":[OSD([sQuery(id+"F67.wireOp",EDGE,"E87")])],"isStart":false});
            chamfer(context, id + "F69", {"entities" : qUnion([Q0, Q1, Q2]), "width" : 0.33 * mm, "tangentPropagation" : true});
        }
        {
            var Q0;
            Q0=makeQuery(id+"F68.opExtrude","CAP_FACE",FACE,{"disambiguationData":[OSD([sQuery(id+"F67.wireOp",EDGE,"E87"),sQuery(id+"F67.wireOp",EDGE,"E88")])],"isStart":false});
            var sketch = newSketch(context, id + "F70", { "sketchPlane" : qUnion([Q0])});
            skCircle(sketch, "E89", {"center": v(0.33, -11.42) * mm, "radius": 3.5 * mm});
            skSolve(sketch);
        }
        {
            var Q0;
            Q0=qSketchRegion(id+"F70",true);
            extrude(context, id + "F71", {"entities" : qUnion([Q0]), "operationType" : NewBodyOperationType.ADD, "depth" : 4.75 * mm, "offsetDistance" : 25 * mm});
        }
        {
            var Q0;
            Q0=makeQuery(id+"F71.opExtrude","CAP_EDGE",EDGE,{"disambiguationData":[OSD([sQuery(id+"F70.wireOp",EDGE,"E89")])],"isStart":false});
            fillet(context, id + "F72", {"entities" : qUnion([Q0]), "radius" : 3.5 * mm, "tangentPropagation" : true, "allowEdgeOverflow" : false});
        }
        {
            var Q0;
            Q0=makeQuery(id+"F68.opExtrude","CAP_FACE",FACE,{"disambiguationData":[OSD([sQuery(id+"F67.wireOp",EDGE,"E87"),sQuery(id+"F67.wireOp",EDGE,"E88")])],"isStart":true});
            var sketch = newSketch(context, id + "F73", { "sketchPlane" : qUnion([Q0])});
            skCircle(sketch, "E90.cCircle", {"center": v(-0.33, -11.42) * mm, "radius": 3.5 * mm, "construction": true});
            skLineSegment(sketch, "E90.0", {"start": v(3.17, -9.4) * mm, "end": v(3.17, -13.44) * mm});
            skLineSegment(sketch, "E90.1", {"start": v(3.17, -13.44) * mm, "end": v(-0.33, -15.47) * mm});
            skLineSegment(sketch, "E90.2", {"start": v(-0.33, -15.47) * mm, "end": v(-3.83, -13.44) * mm});
            skLineSegment(sketch, "E90.3", {"start": v(-3.83, -13.44) * mm, "end": v(-3.83, -9.4) * mm});
            skLineSegment(sketch, "E90.4", {"start": v(-3.83, -9.4) * mm, "end": v(-0.33, -7.38) * mm});
            skLineSegment(sketch, "E90.5", {"start": v(-0.33, -7.38) * mm, "end": v(3.17, -9.4) * mm});
            skPoint(sketch, "E90.0.midPoint", {"position": v(3.17, -11.42) * mm});
            skCircle(sketch, "E91", {"center": v(-0.33, -11.42) * mm, "radius": 6.02 * mm});
            skSolve(sketch);
        }
        {
            var Q0;
            Q0=qSketchRegion(id+"F73",true);
            extrude(context, id + "F74", {"entities" : qUnion([Q0]), "operationType" : NewBodyOperationType.REMOVE, "oppositeDirection" : true, "depth" : 25 * mm, "offsetDistance" : 25 * mm});
        }
        {
            var Q0;
            Q0=qCreatedBy(makeId("Front.planeOp"),FACE);
            var sketch = newSketch(context, id + "F75", { "sketchPlane" : qUnion([Q0])});
            skCircle(sketch, "E92", {"center": v(-14.67, -11.95) * mm, "radius": 6 * mm});
            skCircle(sketch, "E93", {"center": v(-14.67, -11.95) * mm, "radius": 2.08 * mm});
            skSolve(sketch);
        }
        {
            var Q0;
            Q0=qSketchRegion(id+"F75",true);
            extrude(context, id + "F76", {"entities" : qUnion([Q0]), "depth" : 0.5 * mm, "offsetDistance" : 25 * mm, "hasSecondDirection" : true, "secondDirectionOppositeDirection" : true, "secondDirectionDepth" : 2.5 * mm});
        }
        {
            var Q0;
            Q0=qCreatedBy(makeId("Front.planeOp"),FACE);
            var sketch = newSketch(context, id + "F77", { "sketchPlane" : qUnion([Q0])});
            skCircle(sketch, "E94", {"center": v(-14.67, -11.95) * mm, "radius": 4 * mm});
            skSolve(sketch);
        }
        {
            var Q0;
            Q0=qSketchRegion(id+"F77",true);
            extrude(context, id + "F78", {"entities" : qUnion([Q0]), "operationType" : NewBodyOperationType.REMOVE, "oppositeDirection" : true, "depth" : 25 * mm, "offsetDistance" : 25 * mm, "hasDraft" : true, "draftAngle" : 45 * degree, "draftPullDirection" : true, "hasSecondDirection" : true, "secondDirectionOppositeDirection" : false, "secondDirectionDepth" : 25 * mm});
        }
        {
            var Q0;
            Q0=makeQuery(id+"F76.opExtrude","CAP_EDGE",EDGE,{"disambiguationData":[OSD([sQuery(id+"F75.wireOp",EDGE,"E92")])],"isStart":false});
            var Q1;
            Q1=makeQuery(id+"F76.opExtrude","CAP_EDGE",EDGE,{"disambiguationData":[OSD([sQuery(id+"F75.wireOp",EDGE,"E92")])],"isStart":true});
            chamfer(context, id + "F79", {"entities" : qUnion([Q0, Q1]), "width" : 0.2 * mm, "tangentPropagation" : true});
        }
        {
            var Q0;
            Q0=qCreatedBy(makeId("Top.planeOp"),FACE);
            var sketch = newSketch(context, id + "F80", { "sketchPlane" : qUnion([Q0])});
            skLineSegment(sketch, "E95", {"start": v(93, -11.43) * mm, "end": v(89.2, -11.43) * mm});
            skLineSegment(sketch, "E96", {"start": v(89.2, -11.43) * mm, "end": v(89.2, -10.93) * mm});
            skLineSegment(sketch, "E97", {"start": v(89.2, -10.93) * mm, "end": v(91, -9.13) * mm});
            skLineSegment(sketch, "E98", {"start": v(91, -9.13) * mm, "end": v(91, 18.22) * mm});
            skLineSegment(sketch, "E99", {"start": v(91, 18.22) * mm, "end": v(91.36, 18.57) * mm});
            skLineSegment(sketch, "E100", {"start": v(91.36, 18.57) * mm, "end": v(93, 18.57) * mm});
            skLineSegment(sketch, "E101", {"start": v(93, 18.57) * mm, "end": v(93, -11.43) * mm});
            skSolve(sketch);
        }
        {
            var Q0;
            Q0=qSketchRegion(id+"F80",true);
            var Q1;
            Q1=sQuery(id+"F80.wireOp",EDGE,"E101");
            revolve(context, id + "F81", {"entities" : qUnion([Q0]), "axis" : qUnion([Q1]), "revolveType" : RevolveType.FULL});
        }
        {
            var Q0;
            Q0=makeQuery(id+"F81.opRevolve","SWEPT_FACE",FACE,{"disambiguationData":[OSD([sQuery(id+"F80.wireOp",EDGE,"E95")])]});
            var sketch = newSketch(context, id + "F82", { "sketchPlane" : qUnion([Q0])});
            skCircle(sketch, "E102.cCircle", {"center": v(93, 0) * mm, "radius": 1.25 * mm, "construction": true});
            skLineSegment(sketch, "E102.0", {"start": v(92.74, 1.42) * mm, "end": v(94.1, 0.94) * mm});
            skLineSegment(sketch, "E102.1", {"start": v(94.1, 0.94) * mm, "end": v(94.36, -0.48) * mm});
            skLineSegment(sketch, "E102.2", {"start": v(94.36, -0.48) * mm, "end": v(93.27, -1.42) * mm});
            skLineSegment(sketch, "E102.3", {"start": v(93.27, -1.42) * mm, "end": v(91.9, -0.94) * mm});
            skLineSegment(sketch, "E102.4", {"start": v(91.9, -0.94) * mm, "end": v(91.64, 0.48) * mm});
            skLineSegment(sketch, "E102.5", {"start": v(91.64, 0.48) * mm, "end": v(92.74, 1.42) * mm});
            skPoint(sketch, "E102.0.midPoint", {"position": v(93.42, 1.18) * mm});
            skSolve(sketch);
        }
        {
            var Q0;
            Q0=qSketchRegion(id+"F82",true);
            extrude(context, id + "F83", {"entities" : qUnion([Q0]), "operationType" : NewBodyOperationType.REMOVE, "oppositeDirection" : true, "depth" : 1.8 * mm, "offsetDistance" : 25 * mm});
        }
    });
